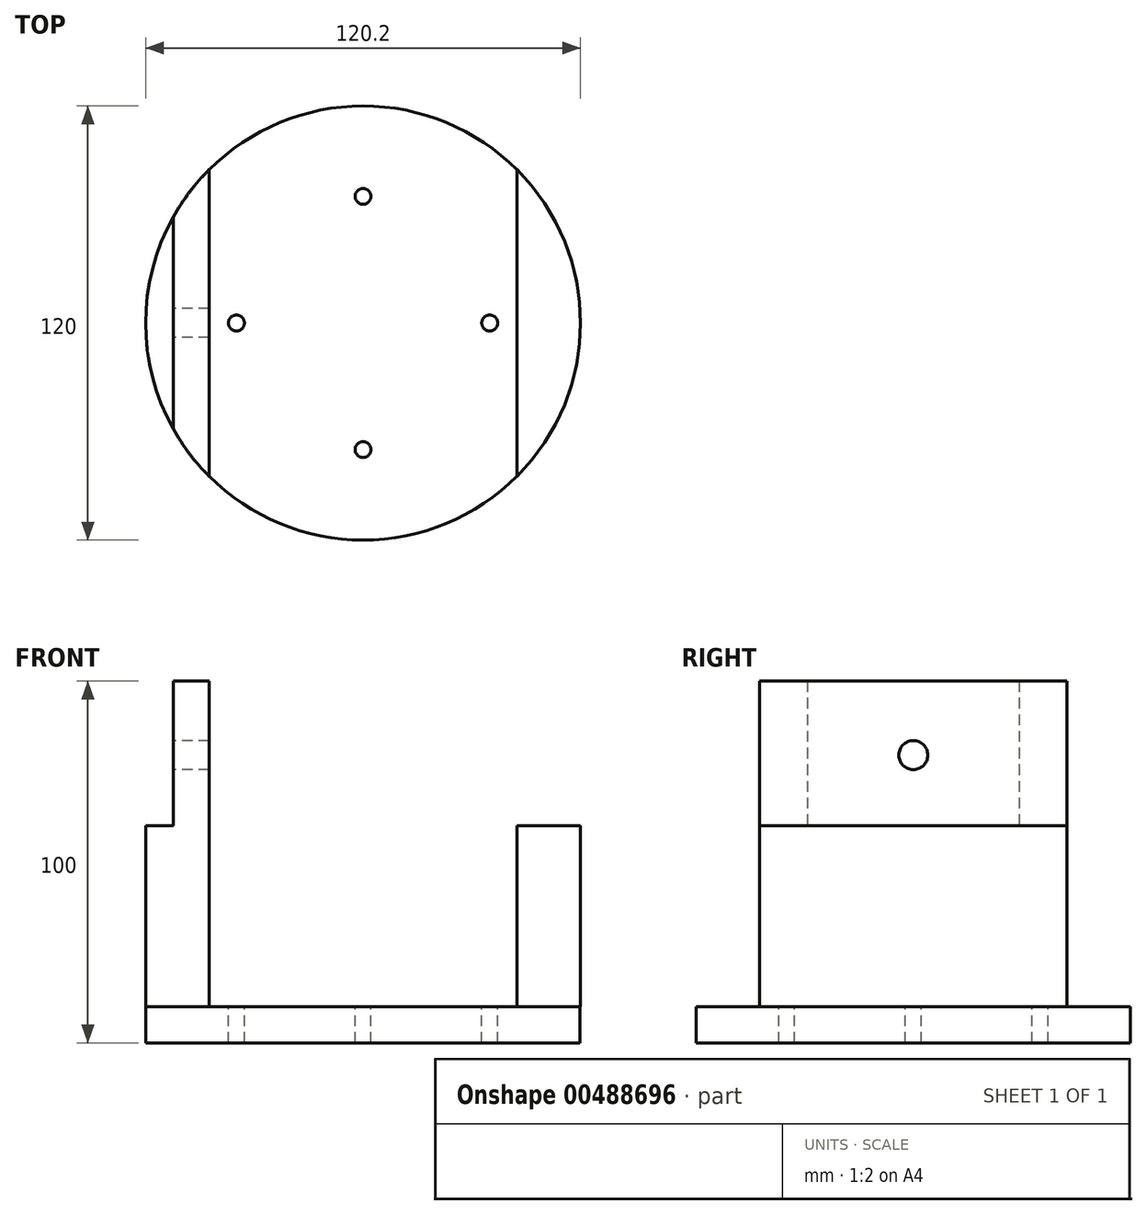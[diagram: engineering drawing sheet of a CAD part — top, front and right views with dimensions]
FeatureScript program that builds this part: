
annotation { "Feature Type Name" : "Feature", "Feature Type Description" : "" }
export const myFeature = defineFeature(function(context is Context, id is Id, definition is map)
    precondition{}
    {
        {
            var Q0;
            Q0=qCreatedBy(makeId("Top.planeOp"),FACE);
            var sketch = newSketch(context, id + "F0", { "sketchPlane" : qUnion([Q0])});
            skCircle(sketch, "E0", {"center": v(0, 0) * mm, "radius": 60 * mm});
            skSolve(sketch);
        }
        {
            var Q0;
            Q0=qSketchRegion(id+"F0",true);
            extrude(context, id + "F1", {"entities" : qUnion([Q0]), "depth" : 10 * mm, "offsetDistance" : 25 * mm});
        }
        {
            var Q0;
            Q0=makeQuery(id+"F1.opExtrude","CAP_FACE",FACE,{"disambiguationData":[OSD([sQuery(id+"F0.wireOp",EDGE,"E0")])],"isStart":false});
            var sketch = newSketch(context, id + "F2", { "sketchPlane" : qUnion([Q0])});
            skCircle(sketch, "E1", {"center": v(0, 0) * mm, "radius": 35 * mm, "construction": true});
            skCircle(sketch, "E2", {"center": v(0, 35) * mm, "radius": 2.2 * mm});
            skCircle(sketch, "E3", {"center": v(35, 0) * mm, "radius": 2.2 * mm});
            skCircle(sketch, "E4", {"center": v(-35, 0) * mm, "radius": 2.2 * mm});
            skCircle(sketch, "E5", {"center": v(0, -35) * mm, "radius": 2.2 * mm});
            skSolve(sketch);
        }
        {
            var Q0;
            Q0=qSketchRegion(id+"F2",true);
            extrude(context, id + "F3", {"entities" : qUnion([Q0]), "operationType" : NewBodyOperationType.REMOVE, "oppositeDirection" : true, "depth" : 14 * mm, "offsetDistance" : 25 * mm});
        }
        {
            var Q0;
            Q0=makeQuery(id+"F1.opExtrude","CAP_FACE",FACE,{"disambiguationData":[OSD([sQuery(id+"F0.wireOp",EDGE,"E0")])],"isStart":false});
            var sketch = newSketch(context, id + "F4", { "sketchPlane" : qUnion([Q0])});
            skLineSegment(sketch, "E6.left", {"start": v(42.5, 42.5) * mm, "end": v(42.5, -42.5) * mm});
            skPoint(sketch, "E6.middle", {"position": v(0, 0) * mm});
            skPoint(sketch, "E6.bottom.end.orphan", {"position": v(-42.5, 42.5) * mm});
            skPoint(sketch, "E7.orphan", {"position": v(42.5, 42.5) * mm});
            skPoint(sketch, "E6.top.start.orphan", {"position": v(42.5, -42.5) * mm});
            skPoint(sketch, "E8.orphan", {"position": v(-42.5, -42.5) * mm});
            skArc(sketch, "E9", {"start": v(-42.5, 42.5) * mm, "mid": v(-60.1, 0) * mm, "end": v(-42.5, -42.5) * mm});
            skArc(sketch, "E10.trimOffspring", {"start": v(42.5, -42.5) * mm, "mid": v(60.1, 0) * mm, "end": v(42.5, 42.5) * mm});
            skLineSegment(sketch, "E11", {"start": v(-42.5, 42.5) * mm, "end": v(-42.5, -42.5) * mm});
            skSolve(sketch);
        }
        {
            var Q0;
            Q0 = qSketchRegion(id + "F4", true);
            extrude(context, id + "F5", {"entities" : qUnion([Q0]), "operationType" : NewBodyOperationType.ADD, "depth" : 50 * mm, "offsetDistance" : 25 * mm});
        }
        {
            var Q0;
            Q0=makeQuery(id+"F5.opExtrude","CAP_FACE",FACE,{"disambiguationData":[OSD([sQuery(id+"F4.wireOp",EDGE,"E9"),sQuery(id+"F4.wireOp",EDGE,"E11")])],"isStart":false});
            var sketch = newSketch(context, id + "F6", { "sketchPlane" : qUnion([Q0])});
            skLineSegment(sketch, "E12.left", {"start": v(-42.5, 42.5) * mm, "end": v(-42.5, -42.5) * mm});
            skLineSegment(sketch, "E12.right", {"start": v(-52.5, 29.26) * mm, "end": v(-52.5, -29.26) * mm});
            skArc(sketch, "E13", {"start": v(-42.5, 42.5) * mm, "mid": v(-47.96, 36.23) * mm, "end": v(-52.5, 29.26) * mm});
            skArc(sketch, "E14.trimOffspring", {"start": v(-52.5, -29.26) * mm, "mid": v(-47.96, -36.23) * mm, "end": v(-42.5, -42.5) * mm});
            skSolve(sketch);
        }
        {
            var Q0;
            Q0 = qSketchRegion(id + "F6", true);
            extrude(context, id + "F7", {"entities" : qUnion([Q0]), "operationType" : NewBodyOperationType.ADD, "depth" : 40 * mm, "offsetDistance" : 25 * mm});
        }
        {
            var Q0;
            Q0=makeQuery(id+"F7.opExtrude","SWEPT_FACE",FACE,{"disambiguationData":[OSD([sQuery(id+"F6.wireOp",EDGE,"E12.right")])]});
            var sketch = newSketch(context, id + "F8", { "sketchPlane" : qUnion([Q0])});
            skLineSegment(sketch, "E15.bottom", {"start": v(-20, 60) * mm, "end": v(38, 60) * mm, "construction": true});
            skLineSegment(sketch, "E15.top", {"start": v(-20, 100) * mm, "end": v(38, 100) * mm, "construction": true});
            skLineSegment(sketch, "E15.left", {"start": v(-20, 60) * mm, "end": v(-20, 100) * mm, "construction": true});
            skLineSegment(sketch, "E15.right", {"start": v(38, 60) * mm, "end": v(38, 100) * mm, "construction": true});
            skCircle(sketch, "E16", {"center": v(0, 79.54) * mm, "radius": 4 * mm});
            skCircle(sketch, "E17", {"center": v(-11, 93.97) * mm, "radius": 2.2 * mm, "construction": true});
            skCircle(sketch, "E18", {"center": v(29, 94.45) * mm, "radius": 2.2 * mm, "construction": true});
            skSolve(sketch);
        }
        {
            var Q0;
            Q0 = qSketchRegion(id + "F8", true);
            extrude(context, id + "F9", {"entities" : qUnion([Q0]), "operationType" : NewBodyOperationType.REMOVE, "oppositeDirection" : true, "depth" : 10 * mm, "offsetDistance" : 25 * mm});
        }
    });
